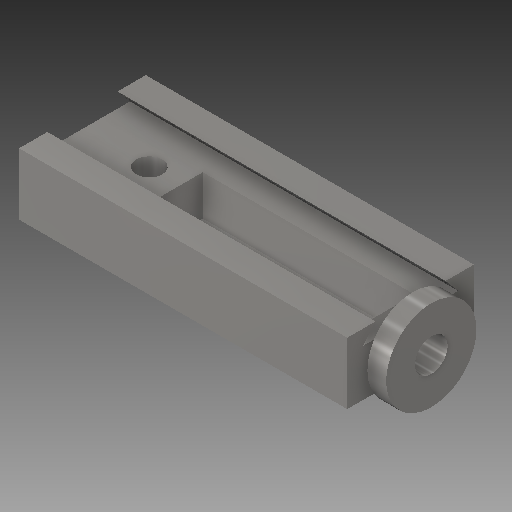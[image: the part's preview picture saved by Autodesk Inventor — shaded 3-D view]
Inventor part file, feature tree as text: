
AUTODESK INVENTOR PART (.ipt)
format: ipt  version: 2018 (Build 220112000, 112)  size: 242,688 bytes
history: native  units: mm
features: extrude x10, sketch x10
ambient origin geometry x8: Origin, YZ Plane, XZ Plane, XY Plane, X Axis, Y Axis, Z Axis, Center Point
bodies: Solid1 (feature_tree)
feature tree (20):
  extrude  "Extrusion1"  Depth=41.4mm
  extrude  "Extrusion2"  Depth=220.0mm
  extrude  "Extrusion3"  Depth=301.25mm TaperAngle=0.0deg
  extrude  "Extrusion4"  Depth=15.1mm
  extrude  "Extrusion5"  Depth=26.9mm TaperAngle=0.0deg
  extrude  "Extrusion6"  Depth=30.2mm
  extrude  "Extrusion7"  Depth=11.0mm
  extrude  "Extrusion8"  Depth=60.4mm
  extrude  "Extrusion9"  Depth=12.7mm
  extrude  "Extrusion10"  TaperAngle=90.0deg  [1 undecoded]
  sketch  "Sketch1"  dims[d0=85.0mm d1=41.4mm]
  sketch  "Sketch2"  dims[d2=220.0mm d3=0.0mm d4=19.0mm]
  sketch  "Sketch3"  dims[d8=19.0mm d9=301.25mm d10=0.0mm]
  sketch  "Sketch5"  dims[d12=15.1mm d13=15.1mm]
  sketch  "Sketch7"  dims[d14=141.9mm d15=26.9mm d16=0.0mm]
  sketch  "Sketch8"  dims[d17=28.6mm d18=30.2mm]
  sketch  "Sketch9"  dims[d19=4.6mm d21=11.0mm]
  sketch  "Sketch10"  dims[d22=91.9mm d23=0.0mm d24=60.4mm]
  sketch  "Sketch11"  dims[d25=12.7mm d26=0.0mm d27=10.6mm]
  sketch  "Sketch12"  dims[d28=83.6mm d29=90.0deg d30=4.9mm d31=6.0mm d32=0.0mm d33=22.0mm d34=22.3mm d35=22.7mm d36=22.15mm d37=0.0mm d38=4.6mm d39=0.0mm d40=17.5mm d41=310.85mm d42=0.0mm d43=4.4mm d44=5.0mm d45=4.4mm d46=2.5mm d47=3.5mm d48=0.0mm d49=40.7mm d50=9.4mm d51=4.0mm d52=40.7mm d53=9.4mm d54=4.0mm d55=70.6mm d56=39.5mm d57=4.5mm d58=4.5mm d59=7.0mm d60=0.0mm d61=8.726646mm d63=8.726646mm d64=10.0mm]
note: 1 required parameter value undecoded (feature->parameter linkage not recoverable at this tier; creation-order binding heuristic only, values carry confidence <= 0.55)
